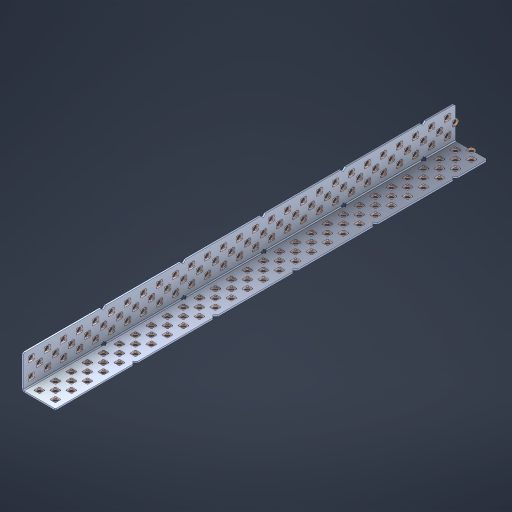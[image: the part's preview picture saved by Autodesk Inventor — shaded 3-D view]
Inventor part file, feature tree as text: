
AUTODESK INVENTOR PART (.ipt)
format: ipt  version: 2023 (Build 270158000, 158)  size: 1,920,512 bytes
history: native  units: in
note: dims shown in document units (in); Inventor stores cm internally (conversion verified against a paired STEP export)
features: other x168, extrude x160, sheet_metal_op x8, sketch x7, pattern_linear x2, mirror x1, chamfer x1
ambient origin geometry x8: Origin, YZ Plane, XZ Plane, XY Plane, X Axis, Y Axis, Z Axis, Center Point
bodies: Solid1 (feature_tree), Body (feature_tree)
feature tree (347):
  sheet_metal_op  "Flanges"
  sheet_metal_op  "Body Pattern"
  pattern_linear  "Center Pattern"  Spacing1=1.0in  [1 undecoded]
  other  "Arc Length"
  pattern_linear  "Notch Pattern"  Spacing1=0.1875in  [1 undecoded]
  other  "Diagonal Plane"
  mirror  "Everything Mirrored"
  chamfer  "End Chamfer"
  sketch  "Sketch1"  dims[d0=1.0in]
  other  "Plate1"
  sketch  "Sketch2"  dims[d1=13.5in]
  other  "Plate2"
  sheet_metal_op  "Bend1"
  sheet_metal_op  "Corner1"
  sketch  "Sketch8"  dims[d2=0.0469in]
  sketch  "Sketch9"  dims[d3=0.0469in]
  other  "Srf91"
  sheet_metal_op  "Body Pattern Sketch"
  other  "Srf92"
  sketch  "Sketch13"  dims[d4=0.0234in]
  sketch  "Sketch15"  dims[d5=0.0938in]
  sketch  "Sketch16"  dims[d6=0.0469in d7=1.0in d8=90.0deg d9=0.0312in d10=0.1875in d11=0.0469in d12=0.0469in d49=0.182in d50=0.02in d52=0.25in d53=0.0469in d54=0.0in d55=0.172in d56=1.0in d57=0.0in d60=10.6299in d62=0.5in d63=0.7874in d65=0.5in d85=0.1473in d86=0.1659in d89=0.0469in d90=0.0in d91=0.04in d92=0.0491in d95=2.5in d96=0.04in d97=0.25in d98=45.0deg d99=0.25in d106=0.182in d107=0.02in d108=0.5in d110=0.0469in d111=0.0in d112=0.172in d113=0.5in d114=0.0in d117=0.5in d123=0.25in d125=0.25in d126=0.0491in d127=0.1227in d128=0.08in d129=0.04in d130=2.5in]
  other  "Srf786"
  other  "Srf856"
  other  "Srf857"
  other  "Srf858"
  other  "Srf859"
  other  "Srf860"
  other  "Srf861"
  other  "Srf889"
  other  "Srf890"
  other  "Srf891"
  other  "Srf1275"
  other  "Srf1276"
  other  "Srf1278"
  other  "Srf1279"
  other  "Srf1280"
  other  "Srf1281"
  other  "Srf1282"
  other  "Srf1283"
  other  "Srf1277"
  other  "Srf1285"
  other  "Srf1286"
  other  "Srf1287"
  other  "Srf1383"
  other  "Srf1384"
  other  "Srf1385"
  other  "Srf1386"
  other  "Srf1387"
  other  "Srf1388"
  other  "Srf1389"
  other  "Srf1390"
  other  "Srf1391"
  other  "Srf1392"
  other  "Srf1393"
  other  "Srf1394"
  other  "Srf1395"
  other  "Srf1396"
  other  "Srf1397"
  other  "Srf1398"
  other  "Srf1399"
  other  "Srf1400"
  other  "Srf1401"
  other  "Srf1402"
  other  "Srf1403"
  other  "Srf1404"
  other  "Srf1405"
  other  "Srf1406"
  other  "Srf1407"
  other  "Srf1408"
  other  "Srf1409"
  other  "Srf1410"
  other  "Srf1411"
  other  "Srf1412"
  other  "Srf1413"
  other  "Srf1414"
  other  "Srf1415"
  other  "Srf1416"
  other  "Srf1417"
  other  "Srf1418"
  other  "Srf1419"
  other  "Srf1420"
  other  "Srf1421"
  other  "Srf1422"
  other  "Srf1423"
  other  "Srf1424"
  other  "Srf1425"
  other  "Srf1426"
  other  "Srf1427"
  other  "Srf1428"
  other  "Srf1445"
  other  "Srf1446"
  other  "Srf1447"
  other  "Srf1448"
  other  "Srf1449"
  other  "Srf1450"
  other  "Srf1451"
  other  "Srf1452"
  other  "Srf1453"
  other  "Srf1454"
  other  "Srf1455"
  other  "Srf1456"
  other  "Srf1457"
  other  "Srf1458"
  other  "Srf1459"
  other  "Srf1460"
  other  "Srf1461"
  other  "Srf1462"
  other  "Srf1463"
  other  "Srf1464"
  other  "Srf1465"
  other  "Srf1466"
  other  "Srf1467"
  other  "Srf1475"
  other  "Srf1476"
  other  "Srf1477"
  other  "Srf1478"
  other  "Srf1479"
  other  "Srf1480"
  other  "Srf1481"
  other  "Srf1482"
  other  "Srf1483"
  other  "Srf1484"
  other  "Srf1485"
  other  "Srf1486"
  other  "Srf1487"
  other  "Srf1488"
  other  "Srf1489"
  other  "Srf1490"
  other  "Srf1491"
  other  "Srf1492"
  other  "Srf1493"
  other  "Srf1494"
  other  "Srf1495"
  other  "Srf1496"
  other  "Srf1497"
  other  "Srf1498"
  other  "Srf1499"
  other  "Srf1500"
  other  "Srf1501"
  other  "Srf1502"
  other  "Srf1503"
  other  "Srf1504"
  other  "Srf1505"
  other  "Srf1506"
  other  "Srf1507"
  other  "Srf1508"
  other  "Srf1509"
  other  "Srf1510"
  other  "Srf1511"
  other  "Srf1512"
  other  "Srf1513"
  other  "Srf1514"
  other  "Srf1515"
  other  "Srf1516"
  other  "Srf1517"
  other  "Srf1518"
  other  "Srf1519"
  other  "Srf1520"
  other  "Srf1537"
  other  "Srf1538"
  other  "Srf1539"
  other  "Srf1540"
  other  "Srf1541"
  other  "Srf1542"
  other  "Srf1543"
  other  "Srf1544"
  other  "Srf1545"
  other  "Srf1546"
  other  "Srf1547"
  other  "Srf1548"
  other  "Srf1549"
  other  "Srf1550"
  other  "Srf1551"
  other  "Srf1552"
  other  "Srf1553"
  other  "Srf1554"
  other  "Srf1555"
  other  "Srf1556"
  other  "Srf1557"
  other  "Srf1558"
  other  "Srf1559"
  sheet_metal_op  "Body Stamp"
  sheet_metal_op  "Body Circle"
  other  "Center Stamp"
  other  "Center Circle"
  sheet_metal_op  "Notch"
  extrude  "ExtrusionSrf92"  Depth=0.0469in
  extrude  "ExtrusionSrf856"  Depth=0.0469in
  extrude  "ExtrusionSrf857"  Depth=0.182in
  extrude  "ExtrusionSrf858"  Depth=0.02in
  extrude  "ExtrusionSrf859"  Depth=0.25in
  extrude  "ExtrusionSrf860"  Depth=0.0469in
  extrude  "ExtrusionSrf861"  TaperAngle=0.0deg  [1 undecoded]
  extrude  "ExtrusionSrf889"  Depth=2.5in
  extrude  "ExtrusionSrf890"  Depth=1.0in TaperAngle=0.0deg
  extrude  "ExtrusionSrf891"  Depth=2.5in
  extrude  "ExtrusionSrf1275"  Depth=0.5in
  extrude  "ExtrusionSrf1276"  Depth=2.5in
  extrude  "ExtrusionSrf1277"  Depth=2.5in
  extrude  "ExtrusionSrf1278"  Depth=0.0469in
  extrude  "ExtrusionSrf1279"  Depth=2.5in TaperAngle=0.0deg
  extrude  "ExtrusionSrf1280"  Depth=2.5in
  extrude  "ExtrusionSrf1281"  Depth=0.25in TaperAngle=45.0deg
  extrude  "ExtrusionSrf1282"  Depth=0.25in
  extrude  "ExtrusionSrf1345"  Depth=0.182in
  extrude  "ExtrusionSrf1346"  Depth=0.02in
  extrude  "ExtrusionSrf1347"  Depth=0.5in
  extrude  "ExtrusionSrf1348"  Depth=0.0469in
  extrude  "ExtrusionSrf1383"  TaperAngle=0.0deg  [1 undecoded]
  extrude  "ExtrusionSrf1384"  Depth=2.5in
  extrude  "ExtrusionSrf1385"  Depth=0.5in TaperAngle=0.0deg
  extrude  "ExtrusionSrf1386"  Depth=0.5in
  extrude  "ExtrusionSrf1387"  Depth=0.25in
  extrude  "ExtrusionSrf1388"  Depth=0.25in
  extrude  "ExtrusionSrf1389"  Depth=2.5in
  extrude  "ExtrusionSrf1390"  Depth=2.5in
  extrude  "ExtrusionSrf1391"  Depth=2.5in
  extrude  "ExtrusionSrf1392"  Depth=2.5in
  extrude  "ExtrusionSrf1393"  Depth=2.5in
  extrude  "ExtrusionSrf1394"  [1 undecoded]
  extrude  "ExtrusionSrf1395"  [1 undecoded]
  extrude  "ExtrusionSrf1396"  [1 undecoded]
  extrude  "ExtrusionSrf1397"  [1 undecoded]
  extrude  "ExtrusionSrf1398"  [1 undecoded]
  extrude  "ExtrusionSrf1399"  [1 undecoded]
  extrude  "ExtrusionSrf1400"  [1 undecoded]
  extrude  "ExtrusionSrf1401"  [1 undecoded]
  extrude  "ExtrusionSrf1402"  [1 undecoded]
  extrude  "ExtrusionSrf1403"  [1 undecoded]
  extrude  "ExtrusionSrf1404"  [1 undecoded]
  extrude  "ExtrusionSrf1405"  [1 undecoded]
  extrude  "ExtrusionSrf1406"  [1 undecoded]
  extrude  "ExtrusionSrf1407"  [1 undecoded]
  extrude  "ExtrusionSrf1408"  [1 undecoded]
  extrude  "ExtrusionSrf1409"  [1 undecoded]
  extrude  "ExtrusionSrf1410"  [1 undecoded]
  extrude  "ExtrusionSrf1411"  [1 undecoded]
  extrude  "ExtrusionSrf1412"  [1 undecoded]
  extrude  "ExtrusionSrf1413"  [1 undecoded]
  extrude  "ExtrusionSrf1414"  [1 undecoded]
  extrude  "ExtrusionSrf1415"  [1 undecoded]
  extrude  "ExtrusionSrf1416"  [1 undecoded]
  extrude  "ExtrusionSrf1417"  [1 undecoded]
  extrude  "ExtrusionSrf1418"  [1 undecoded]
  extrude  "ExtrusionSrf1419"  [1 undecoded]
  extrude  "ExtrusionSrf1420"  [1 undecoded]
  extrude  "ExtrusionSrf1421"  [1 undecoded]
  extrude  "ExtrusionSrf1422"  [1 undecoded]
  extrude  "ExtrusionSrf1423"  [1 undecoded]
  extrude  "ExtrusionSrf1424"  [1 undecoded]
  extrude  "ExtrusionSrf1425"  [1 undecoded]
  extrude  "ExtrusionSrf1426"  [1 undecoded]
  extrude  "ExtrusionSrf1427"  [1 undecoded]
  extrude  "ExtrusionSrf1428"  [1 undecoded]
  extrude  "ExtrusionSrf1445"  [1 undecoded]
  extrude  "ExtrusionSrf1446"  [1 undecoded]
  extrude  "ExtrusionSrf1447"  [1 undecoded]
  extrude  "ExtrusionSrf1448"  [1 undecoded]
  extrude  "ExtrusionSrf1449"  [1 undecoded]
  extrude  "ExtrusionSrf1450"  [1 undecoded]
  extrude  "ExtrusionSrf1451"  [1 undecoded]
  extrude  "ExtrusionSrf1452"  [1 undecoded]
  extrude  "ExtrusionSrf1453"  [1 undecoded]
  extrude  "ExtrusionSrf1454"  [1 undecoded]
  extrude  "ExtrusionSrf1455"  [1 undecoded]
  extrude  "ExtrusionSrf1456"  [1 undecoded]
  extrude  "ExtrusionSrf1457"  [1 undecoded]
  extrude  "ExtrusionSrf1458"  [1 undecoded]
  extrude  "ExtrusionSrf1459"  [1 undecoded]
  extrude  "ExtrusionSrf1460"  [1 undecoded]
  extrude  "ExtrusionSrf1461"  [1 undecoded]
  extrude  "ExtrusionSrf1462"  [1 undecoded]
  extrude  "ExtrusionSrf1463"  [1 undecoded]
  extrude  "ExtrusionSrf1464"  [1 undecoded]
  extrude  "ExtrusionSrf1465"  [1 undecoded]
  extrude  "ExtrusionSrf1466"  [1 undecoded]
  extrude  "ExtrusionSrf1467"  [1 undecoded]
  extrude  "ExtrusionSrf1475"  [1 undecoded]
  extrude  "ExtrusionSrf1476"  [1 undecoded]
  extrude  "ExtrusionSrf1477"  [1 undecoded]
  extrude  "ExtrusionSrf1478"  [1 undecoded]
  extrude  "ExtrusionSrf1479"  [1 undecoded]
  extrude  "ExtrusionSrf1480"  [1 undecoded]
  extrude  "ExtrusionSrf1481"  [1 undecoded]
  extrude  "ExtrusionSrf1482"  [1 undecoded]
  extrude  "ExtrusionSrf1483"  [1 undecoded]
  extrude  "ExtrusionSrf1484"  [1 undecoded]
  extrude  "ExtrusionSrf1485"  [1 undecoded]
  extrude  "ExtrusionSrf1486"  [1 undecoded]
  extrude  "ExtrusionSrf1487"  [1 undecoded]
  extrude  "ExtrusionSrf1488"  [1 undecoded]
  extrude  "ExtrusionSrf1489"  [1 undecoded]
  extrude  "ExtrusionSrf1490"  [1 undecoded]
  extrude  "ExtrusionSrf1491"  [1 undecoded]
  extrude  "ExtrusionSrf1492"  [1 undecoded]
  extrude  "ExtrusionSrf1493"  [1 undecoded]
  extrude  "ExtrusionSrf1494"  [1 undecoded]
  extrude  "ExtrusionSrf1495"  [1 undecoded]
  extrude  "ExtrusionSrf1496"  [1 undecoded]
  extrude  "ExtrusionSrf1497"  [1 undecoded]
  extrude  "ExtrusionSrf1498"  [1 undecoded]
  extrude  "ExtrusionSrf1499"  [1 undecoded]
  extrude  "ExtrusionSrf1500"  [1 undecoded]
  extrude  "ExtrusionSrf1501"  [1 undecoded]
  extrude  "ExtrusionSrf1502"  [1 undecoded]
  extrude  "ExtrusionSrf1503"  [1 undecoded]
  extrude  "ExtrusionSrf1504"  [1 undecoded]
  extrude  "ExtrusionSrf1505"  [1 undecoded]
  extrude  "ExtrusionSrf1506"  [1 undecoded]
  extrude  "ExtrusionSrf1507"  [1 undecoded]
  extrude  "ExtrusionSrf1508"  [1 undecoded]
  extrude  "ExtrusionSrf1509"  [1 undecoded]
  extrude  "ExtrusionSrf1510"  [1 undecoded]
  extrude  "ExtrusionSrf1511"  [1 undecoded]
  extrude  "ExtrusionSrf1512"  [1 undecoded]
  extrude  "ExtrusionSrf1513"  [1 undecoded]
  extrude  "ExtrusionSrf1514"  [1 undecoded]
  extrude  "ExtrusionSrf1515"  [1 undecoded]
  extrude  "ExtrusionSrf1516"  [1 undecoded]
  extrude  "ExtrusionSrf1517"  [1 undecoded]
  extrude  "ExtrusionSrf1518"  [1 undecoded]
  extrude  "ExtrusionSrf1519"  [1 undecoded]
  extrude  "ExtrusionSrf1520"  [1 undecoded]
  extrude  "ExtrusionSrf1537"  [1 undecoded]
  extrude  "ExtrusionSrf1538"  [1 undecoded]
  extrude  "ExtrusionSrf1539"  [1 undecoded]
  extrude  "ExtrusionSrf1540"  [1 undecoded]
  extrude  "ExtrusionSrf1541"  [1 undecoded]
  extrude  "ExtrusionSrf1542"  [1 undecoded]
  extrude  "ExtrusionSrf1543"  [1 undecoded]
  extrude  "ExtrusionSrf1544"  [1 undecoded]
  extrude  "ExtrusionSrf1545"  [1 undecoded]
  extrude  "ExtrusionSrf1546"  [1 undecoded]
  extrude  "ExtrusionSrf1547"  [1 undecoded]
  extrude  "ExtrusionSrf1548"  [1 undecoded]
  extrude  "ExtrusionSrf1549"  [1 undecoded]
  extrude  "ExtrusionSrf1550"  [1 undecoded]
  extrude  "ExtrusionSrf1551"  [1 undecoded]
  extrude  "ExtrusionSrf1552"  [1 undecoded]
  extrude  "ExtrusionSrf1553"  [1 undecoded]
  extrude  "ExtrusionSrf1554"  [1 undecoded]
  extrude  "ExtrusionSrf1555"  [1 undecoded]
  extrude  "ExtrusionSrf1556"  [1 undecoded]
  extrude  "ExtrusionSrf1557"  [1 undecoded]
  extrude  "ExtrusionSrf1558"  [1 undecoded]
  extrude  "ExtrusionSrf1559"  [1 undecoded]
note: 131 required parameter values undecoded (feature->parameter linkage not recoverable at this tier; creation-order binding heuristic only, values carry confidence <= 0.55)
